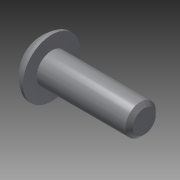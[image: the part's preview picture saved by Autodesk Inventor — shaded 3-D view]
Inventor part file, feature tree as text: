
AUTODESK INVENTOR PART (.ipt)
format: ipt  version: 2015 (Build 190159000, 159)  size: 125,952 bytes
history: native  units: in
note: dims shown in document units (in); Inventor stores cm internally (conversion verified against a paired STEP export)
features: other x3, extrude x1, chamfer x1, imported_body x1, sketch x1
ambient origin geometry x8: Origin, YZ Plane, XZ Plane, XY Plane, X Axis, Y Axis, Z Axis, Center Point
bodies: Body1 (feature_tree)
feature tree (7):
  other  "Bolt 0.5 inch"
  parser-record x1  (decoder bookkeeping rows leaked as tree rows — omitted from the tree; the rows remain in map.json)
  other  "Bolt"
  extrude  "thread length"  Depth=0.5in TaperAngle=0.0deg
  chamfer  "thread chamfer"  Distance=0.02in Angle=45.0deg
  imported_body  "Base1"
  sketch  "Sketch1"  dims[d0=0.164in d1=0.5in d2=0.0in d3=0.02in d4=0.125in d5=45.0deg d7=0.0in d9=0.0in]
